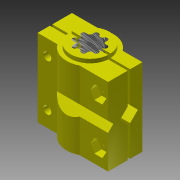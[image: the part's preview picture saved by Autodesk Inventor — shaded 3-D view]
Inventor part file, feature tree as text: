
AUTODESK INVENTOR PART (.ipt)
format: ipt  version: 2013 (Build 170138000, 138)  size: 2,167,296 bytes
history: native  units: mm
features: extrude x6, sketch x4, projected_geometry x4, other x3, pattern_circular x2, thread x1
ambient origin geometry x8: Origin, YZ Plane, XZ Plane, XY Plane, X Axis, Y Axis, Z Axis, Center Point
bodies: Solid1 (feature_tree)
feature tree (20):
  thread  "THREAD CLAMP SETUP.iam"  [1 undecoded]
  other  "_THREAD CLAMP.ipt:1"
  other  "_THREAD CLAMP.ipt:2"
  other  "7_16 TORQSPLINE.ipt:1"
  extrude  "Extrusion8"  Depth=6.35mm
  extrude  "Extrusion2"  Depth=3.0mm TaperAngle=0.0deg
  extrude  "Extrusion3"  Depth=2.6mm
  extrude  "Extrusion4"  Depth=3.0mm TaperAngle=0.0deg
  pattern_circular  "Circular Pattern1"  [2 undecoded]
  extrude  "Extrusion5"  Depth=3.0mm TaperAngle=0.0deg
  extrude  "Extrusion6"  Depth=20.0mm TaperAngle=360.0deg
  pattern_circular  "Circular Pattern2"  [2 undecoded]
  sketch  "Sketch3"  dims[d3=12.7mm d4=0.0mm d5=6.35mm]
  projected_geometry  "Projected Loop3"
  projected_geometry  "Projected Loop4"
  sketch  "Sketch4"  dims[d6=0.5mm d7=0.0mm d8=3.0mm d9=0.0mm]
  sketch  "Sketch5"  dims[d10=20.0mm d11=360.0deg d13=2.6mm]
  projected_geometry  "Projected Loop5"
  sketch  "Sketch8"  dims[d15=2.05mm d16=3.0mm d17=0.0mm d19=12.7mm d20=3.0mm d21=0.0mm d24=20.0mm d25=360.0deg d28=6.25mm d29=0.0mm]
  projected_geometry  "Projected Loop7"
note: 5 required parameter values undecoded (feature->parameter linkage not recoverable at this tier; creation-order binding heuristic only, values carry confidence <= 0.55)
